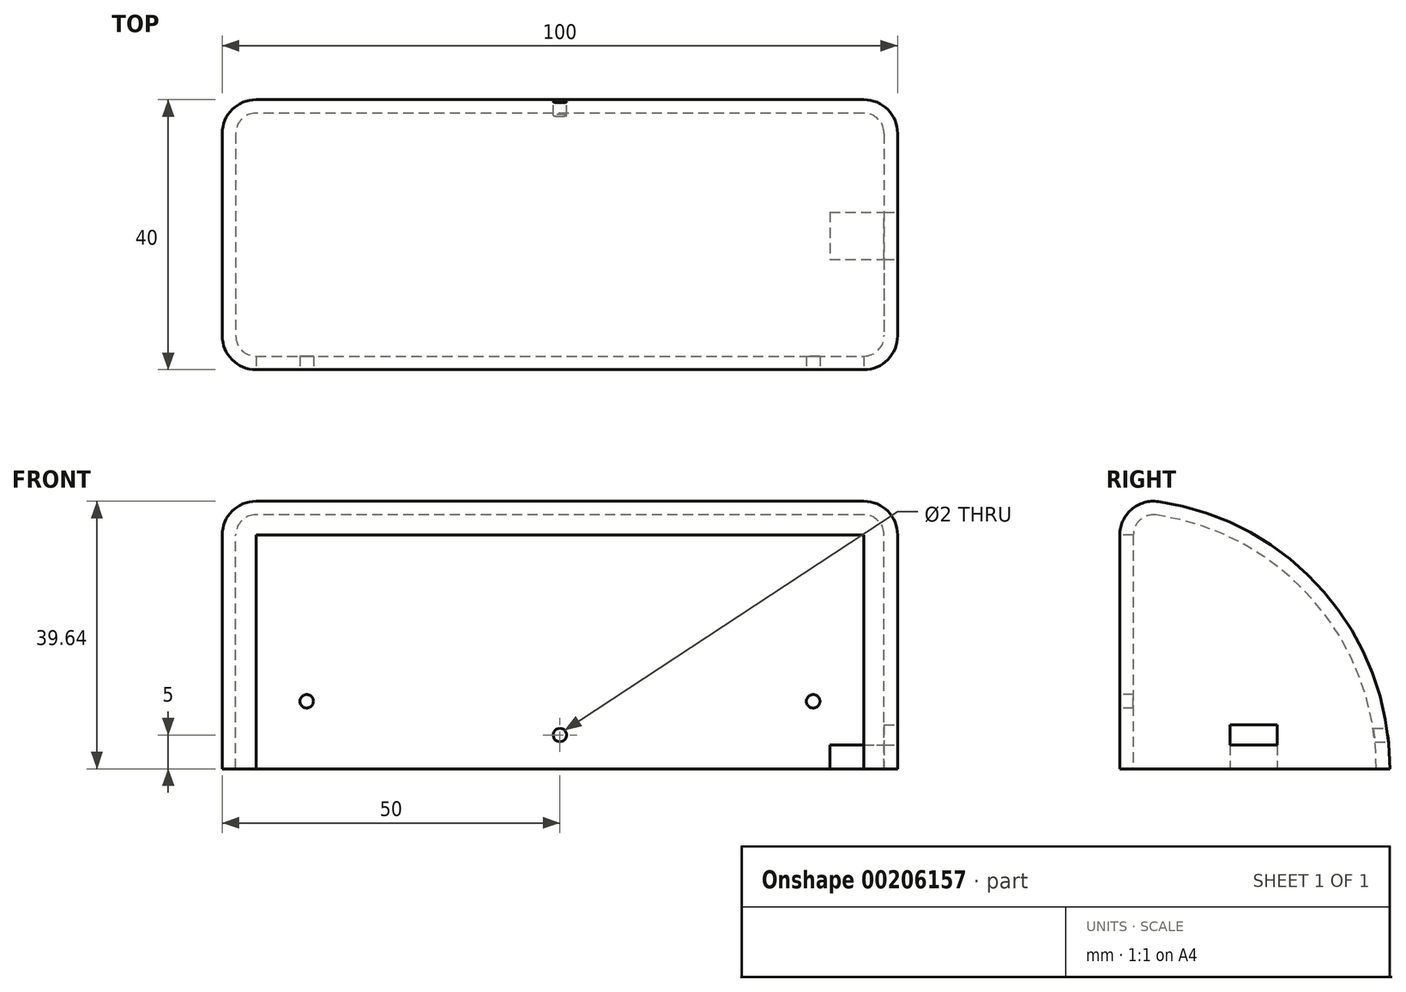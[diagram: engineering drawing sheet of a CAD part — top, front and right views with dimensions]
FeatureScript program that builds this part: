
annotation { "Feature Type Name" : "Feature", "Feature Type Description" : "" }
export const myFeature = defineFeature(function(context is Context, id is Id, definition is map)
    precondition{}
    {
        {
            var Q0;
            Q0=qCreatedBy(makeId("Right.planeOp"),FACE);
            var sketch = newSketch(context, id + "F0", { "sketchPlane" : qUnion([Q0])});
            skLineSegment(sketch, "E0", {"start": v(16.11, 0) * mm, "end": v(-23.89, 0) * mm});
            skLineSegment(sketch, "E1", {"start": v(-23.89, 0) * mm, "end": v(-23.89, 40) * mm});
            skArc(sketch, "E2", {"start": v(16.11, 0) * mm, "mid": v(4.4, 28.28) * mm, "end": v(-23.89, 40) * mm});
            skSolve(sketch);
        }
        {
            var Q0;
            Q0=makeQuery(id+"F0.imprint","IMPRINT",FACE,{"disambiguationData":[TD([[makeQuery(id+"F0.imprint","IMPRINT",EDGE,{"derivedFrom":sQuery(id+"F0.wireOp",EDGE,"E0")}),-1.0]])]});
            extrude(context, id + "F1", {"entities" : qUnion([Q0]), "depth" : 50 * mm});
        }
        {
            var Q0;
            Q0=makeQuery(id+"F1.opExtrude","SWEPT_EDGE",EDGE,{"disambiguationData":[OSD([sQuery(id+"F0.wireOp",EDGE,"E1"),sQuery(id+"F0.wireOp",EDGE,"E2")])]});
            var Q1;
            Q1=makeQuery(id+"F1.opExtrude","CAP_EDGE",EDGE,{"disambiguationData":[OSD([sQuery(id+"F0.wireOp",EDGE,"E2")])],"isStart":false});
            var Q2;
            Q2=makeQuery(id+"F1.opExtrude","CAP_EDGE",EDGE,{"disambiguationData":[OSD([sQuery(id+"F0.wireOp",EDGE,"E1")])],"isStart":false});
            fillet(context, id + "F2", {"entities" : qUnion([Q0, Q1, Q2]), "radius" : 5 * mm, "tangentPropagation" : true, "allowEdgeOverflow" : false});
        }
        {
            var Q0;
            Q0=makeQuery(id+"F1.opExtrude","CAP_FACE",FACE,{"disambiguationData":[OSD([sQuery(id+"F0.wireOp",EDGE,"E0"),sQuery(id+"F0.wireOp",EDGE,"E1"),sQuery(id+"F0.wireOp",EDGE,"E2")])],"isStart":true});
            var Q1;
            Q1=makeQuery(id+"F1.opExtrude","SWEPT_FACE",FACE,{"disambiguationData":[OSD([sQuery(id+"F0.wireOp",EDGE,"E0")])]});
            shell(context, id + "F3", {"entities" : qUnion([Q0, Q1]), "thickness" : 2 * mm});
        }
        {
            var Q0;
            Q0=makeQuery(id+"F1.opExtrude","SWEPT_FACE",FACE,{"disambiguationData":[OSD([sQuery(id+"F0.wireOp",EDGE,"E1")])]});
            var sketch = newSketch(context, id + "F4", { "sketchPlane" : qUnion([Q0])});
            skPoint(sketch, "E3.middle", {"position": v(22.5, 17.32) * mm});
            skLineSegment(sketch, "E4", {"start": v(0, 34.64) * mm, "end": v(45, 0) * mm, "construction": true});
            skCircle(sketch, "E5", {"center": v(22.5, 17.32) * mm, "radius": 14 * mm});
            skCircle(sketch, "E6", {"center": v(7.5, 10) * mm, "radius": 1 * mm});
            skLineSegment(sketch, "E7", {"start": v(22.5, 17.32) * mm, "end": v(22.5, 0) * mm, "construction": true});
            skCircle(sketch, "E8.MirrorC", {"center": v(37.5, 10) * mm, "radius": 1 * mm});
            skSolve(sketch);
        }
        {
            var Q0;
            Q0=makeQuery(id+"F4.imprint","IMPRINT",FACE,{"disambiguationData":[TD([[makeQuery(id+"F4.imprint","IMPRINT",EDGE,{"derivedFrom":sQuery(id+"F4.wireOp",EDGE,"E5")}),1.0]])]});
            var Q1;
            Q1=makeQuery(id+"F4.imprint","IMPRINT",FACE,{"disambiguationData":[TD([[makeQuery(id+"F4.imprint","IMPRINT",EDGE,{"derivedFrom":sQuery(id+"F4.wireOp",EDGE,"E6")}),1.0]])]});
            var Q2;
            Q2=makeQuery(id+"F4.imprint","IMPRINT",FACE,{"disambiguationData":[TD([[makeQuery(id+"F4.imprint","IMPRINT",EDGE,{"derivedFrom":sQuery(id+"F4.wireOp",EDGE,"E8.MirrorC")}),-1.0]])]});
            extrude(context, id + "F5", {"entities" : qUnion([Q0, Q1, Q2]), "operationType" : NewBodyOperationType.REMOVE, "endBound" : BoundingType.UP_TO_NEXT, "oppositeDirection" : true, "depth" : 25 * mm});
        }
        {
            var Q0;
            Q0=makeQuery(id+"F1.opExtrude","SWEPT_BODY",BODY,{"disambiguationData":[OSD([sQuery(id+"F0.wireOp",EDGE,"E0"),sQuery(id+"F0.wireOp",EDGE,"E1"),sQuery(id+"F0.wireOp",EDGE,"E2")])]});
            var Q1;
            Q1=qCreatedBy(makeId("Right.planeOp"),FACE);
            mirror(context, id + "F6", {"operationType" : NewBodyOperationType.ADD, "entities" : qUnion([Q0]), "mirrorPlane" : qUnion([Q1])});
        }
        {
            var Q0;
            Q0=qCreatedBy(makeId("Front.planeOp"),FACE);
            var Q1;
            {var subQ0=sQuery(id+"F0.wireOp",EDGE,"E2");Q1=makeQuery(id+"F6.opPattern","COPY",VERTEX,{"derivedFrom":makeQuery(id+"F2.opFillet","BLEND_VERTEX",VERTEX,{"blendedFrom":[makeQuery(id+"F1.opExtrude","CAP_EDGE",EDGE,{"disambiguationData":[OSD([subQ0])],"isStart":false}),makeQuery(id+"F1.opExtrude","SWEPT_FACE",FACE,{"disambiguationData":[OSD([sQuery(id+"F0.wireOp",EDGE,"E0")])]}),makeQuery(id+"F1.opExtrude","SWEPT_FACE",FACE,{"disambiguationData":[OSD([subQ0])]})],"blendedInto":[makeQuery(id+"F1.opExtrude","SWEPT_FACE",FACE,{"disambiguationData":[OSD([sQuery(id+"F0.wireOp",EDGE,"E0")])]}),makeQuery(id+"F1.opExtrude","SWEPT_FACE",FACE,{"disambiguationData":[OSD([subQ0])]})]}),"instanceName":"1"});}
            cPlane(context, id + "F7", {"entities" : qUnion([Q0, Q1]), "cplaneType" : CPlaneType.PLANE_POINT, "offset" : 25 * mm, "width" : 150 * mm, "height" : 150 * mm});
        }
        {
            var Q0;
            Q0=qCreatedBy(id+"F7.planeOp",FACE);
            var sketch = newSketch(context, id + "F8", { "sketchPlane" : qUnion([Q0])});
            skCircle(sketch, "E9", {"center": v(0, 5) * mm, "radius": 1 * mm});
            skSolve(sketch);
        }
        {
            var Q0;
            Q0=makeQuery(id+"F8.imprint","IMPRINT",FACE,{"disambiguationData":[TD([[makeQuery(id+"F8.imprint","IMPRINT",EDGE,{"derivedFrom":sQuery(id+"F8.wireOp",EDGE,"E9")}),1.0]])]});
            extrude(context, id + "F9", {"entities" : qUnion([Q0]), "operationType" : NewBodyOperationType.REMOVE, "depth" : 10 * mm});
        }
        {
            var Q0;
            Q0=makeQuery(id+"F1.opExtrude","CAP_FACE",FACE,{"disambiguationData":[OSD([sQuery(id+"F0.wireOp",EDGE,"E0"),sQuery(id+"F0.wireOp",EDGE,"E1"),sQuery(id+"F0.wireOp",EDGE,"E2")])],"isStart":false});
            var sketch = newSketch(context, id + "F10", { "sketchPlane" : qUnion([Q0])});
            skLineSegment(sketch, "E10.bottom", {"start": v(-0.57, 3.5) * mm, "end": v(-7.57, 3.5) * mm});
            skLineSegment(sketch, "E10.top", {"start": v(-0.57, 6.5) * mm, "end": v(-7.57, 6.5) * mm});
            skLineSegment(sketch, "E10.left", {"start": v(-0.57, 3.5) * mm, "end": v(-0.57, 6.5) * mm});
            skLineSegment(sketch, "E10.right", {"start": v(-7.57, 3.5) * mm, "end": v(-7.57, 6.5) * mm});
            skPoint(sketch, "E10.middle", {"position": v(-4.07, 5) * mm});
            skLineSegment(sketch, "E11", {"start": v(-18.89, 5) * mm, "end": v(10.75, 5) * mm, "construction": true});
            skSolve(sketch);
        }
        {
            var Q0;
            Q0=makeQuery(id+"F10.imprint","IMPRINT",FACE,{"disambiguationData":[TD([[makeQuery(id+"F10.imprint","IMPRINT",EDGE,{"derivedFrom":sQuery(id+"F10.wireOp",EDGE,"E10.bottom")}),-1.0]])]});
            extrude(context, id + "F11", {"entities" : qUnion([Q0]), "operationType" : NewBodyOperationType.REMOVE, "endBound" : BoundingType.UP_TO_NEXT, "oppositeDirection" : true, "depth" : 25 * mm});
        }
        {
            var Q0;
            Q0=makeQuery(id+"F3.opShell","OFFSET_FACE",FACE,{"disambiguationData":[OSD([sQuery(id+"F0.wireOp",EDGE,"E0"),sQuery(id+"F0.wireOp",EDGE,"E1"),sQuery(id+"F0.wireOp",EDGE,"E2")])]});
            var sketch = newSketch(context, id + "F12", { "sketchPlane" : qUnion([Q0])});
            skLineSegment(sketch, "E12.bottom", {"start": v(0.57, 3.5) * mm, "end": v(7.57, 3.5) * mm});
            skLineSegment(sketch, "E12.top", {"start": v(0.57, 0) * mm, "end": v(7.57, 0) * mm});
            skLineSegment(sketch, "E12.left", {"start": v(0.57, 3.5) * mm, "end": v(0.57, 0) * mm});
            skLineSegment(sketch, "E12.right", {"start": v(7.57, 3.5) * mm, "end": v(7.57, 0) * mm});
            skSolve(sketch);
        }
        {
            var Q0;
            Q0 = qSketchRegion(id + "F12", true);
            extrude(context, id + "F13", {"entities" : qUnion([Q0]), "operationType" : NewBodyOperationType.ADD, "depth" : 8 * mm});
        }
    });
